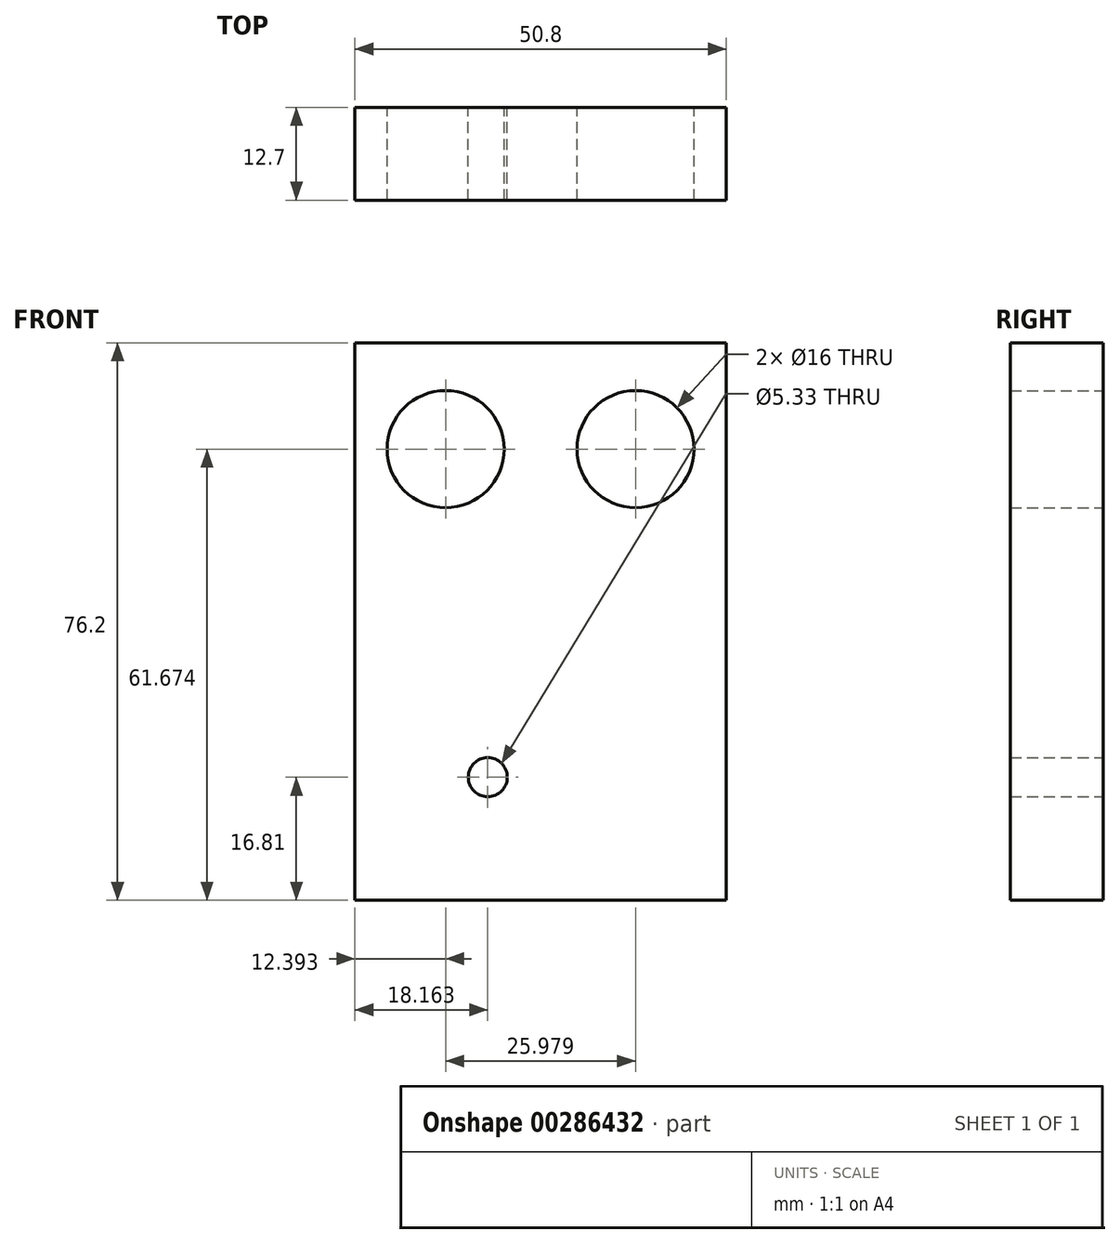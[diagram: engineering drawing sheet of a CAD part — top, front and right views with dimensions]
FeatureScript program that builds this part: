
annotation { "Feature Type Name" : "Feature", "Feature Type Description" : "" }
export const myFeature = defineFeature(function(context is Context, id is Id, definition is map)
    precondition{}
    {
        {
            var Q0;
            Q0=qCreatedBy(makeId("Front.planeOp"),FACE);
            var sketch = newSketch(context, id + "F0", { "sketchPlane" : qUnion([Q0])});
            skLineSegment(sketch, "E0.bottom", {"start": v(-112.14, 59.4) * mm, "end": v(-61.34, 59.4) * mm});
            skLineSegment(sketch, "E0.top", {"start": v(-112.14, -16.8) * mm, "end": v(-61.34, -16.8) * mm});
            skLineSegment(sketch, "E0.left", {"start": v(-112.14, 59.4) * mm, "end": v(-112.14, -16.8) * mm});
            skLineSegment(sketch, "E0.right", {"start": v(-61.34, 59.4) * mm, "end": v(-61.34, -16.8) * mm});
            skCircle(sketch, "E1", {"center": v(-99.75, 44.86) * mm, "radius": 8 * mm});
            skCircle(sketch, "E2", {"center": v(-73.77, 44.86) * mm, "radius": 8 * mm});
            skCircle(sketch, "E3", {"center": v(-93.98, 0) * mm, "radius": 2.67 * mm});
            skSolve(sketch);
        }
        {
            var Q0;
            Q0 = qSketchRegion(id + "F0", true);
            extrude(context, id + "F1", {"entities" : qUnion([Q0]), "depth" : 12.7 * mm});
        }
    });
